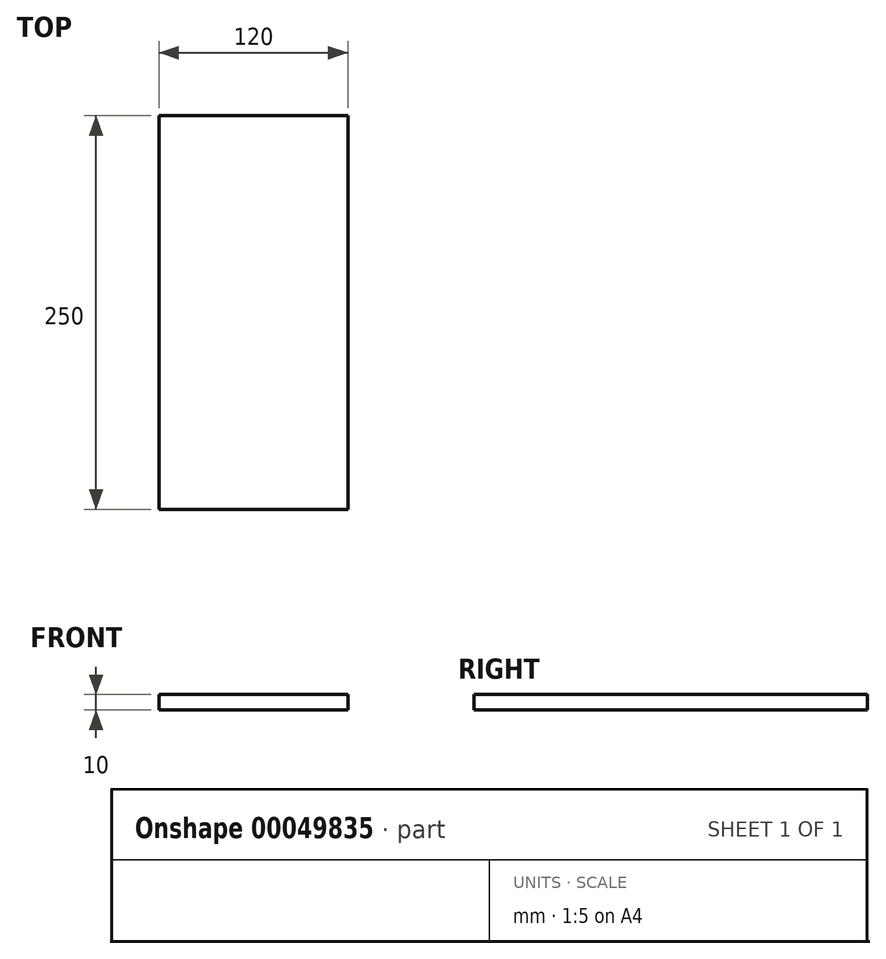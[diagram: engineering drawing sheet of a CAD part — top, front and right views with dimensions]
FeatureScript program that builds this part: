
annotation { "Feature Type Name" : "Feature", "Feature Type Description" : "" }
export const myFeature = defineFeature(function(context is Context, id is Id, definition is map)
    precondition{}
    {
        {
            var Q0;
            Q0=qCreatedBy(makeId("Top.planeOp"),FACE);
            var sketch = newSketch(context, id + "F0", { "sketchPlane" : qUnion([Q0])});
            skLineSegment(sketch, "E0.bottom", {"start": v(-44.88, 108.19) * mm, "end": v(75.12, 108.19) * mm});
            skLineSegment(sketch, "E0.top", {"start": v(-44.88, -141.81) * mm, "end": v(75.12, -141.81) * mm});
            skLineSegment(sketch, "E0.left", {"start": v(-44.88, 108.19) * mm, "end": v(-44.88, -141.81) * mm});
            skLineSegment(sketch, "E0.right", {"start": v(75.12, 108.19) * mm, "end": v(75.12, -141.81) * mm});
            skSolve(sketch);
        }
        {
            var Q0;
            Q0=qSketchRegion(id+"F0",true);
            extrude(context, id + "F1", {"entities" : qUnion([Q0]), "depth" : 10 * mm});
        }
    });
